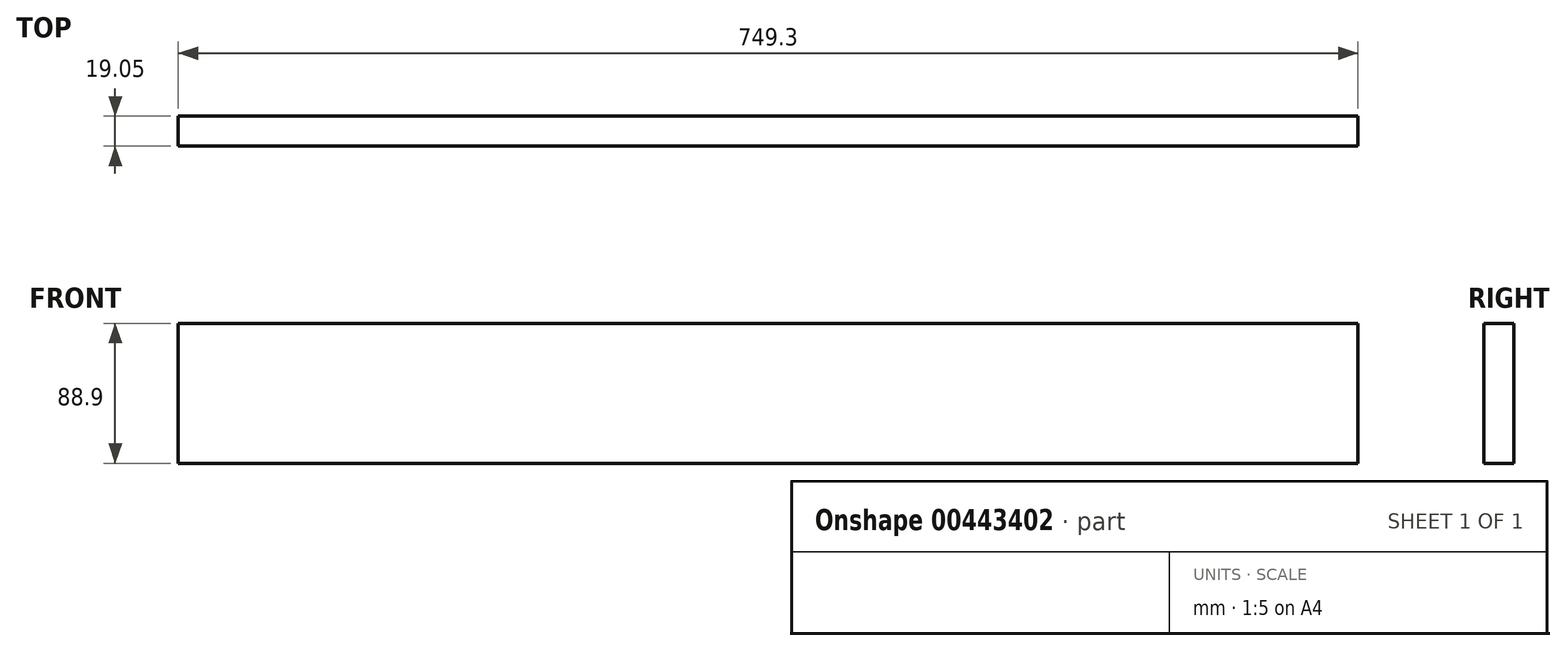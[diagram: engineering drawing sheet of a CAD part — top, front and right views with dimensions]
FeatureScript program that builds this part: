
annotation { "Feature Type Name" : "Feature", "Feature Type Description" : "" }
export const myFeature = defineFeature(function(context is Context, id is Id, definition is map)
    precondition{}
    {
        {
            var Q0;
            Q0=qCreatedBy(makeId("Front.planeOp"),FACE);
            var sketch = newSketch(context, id + "F0", { "sketchPlane" : qUnion([Q0])});
            skLineSegment(sketch, "E0.bottom", {"start": v(374.65, -44.45) * mm, "end": v(-374.65, -44.45) * mm});
            skLineSegment(sketch, "E0.top", {"start": v(374.65, 44.45) * mm, "end": v(-374.65, 44.45) * mm});
            skLineSegment(sketch, "E0.left", {"start": v(374.65, -44.45) * mm, "end": v(374.65, 44.45) * mm});
            skLineSegment(sketch, "E0.right", {"start": v(-374.65, -44.45) * mm, "end": v(-374.65, 44.45) * mm});
            skPoint(sketch, "E0.middle", {"position": v(0, 0) * mm});
            skSolve(sketch);
        }
        {
            var Q0;
            Q0 = qSketchRegion(id + "F0", true);
            extrude(context, id + "F1", {"entities" : qUnion([Q0]), "depth" : 19.05 * mm});
        }
    });
